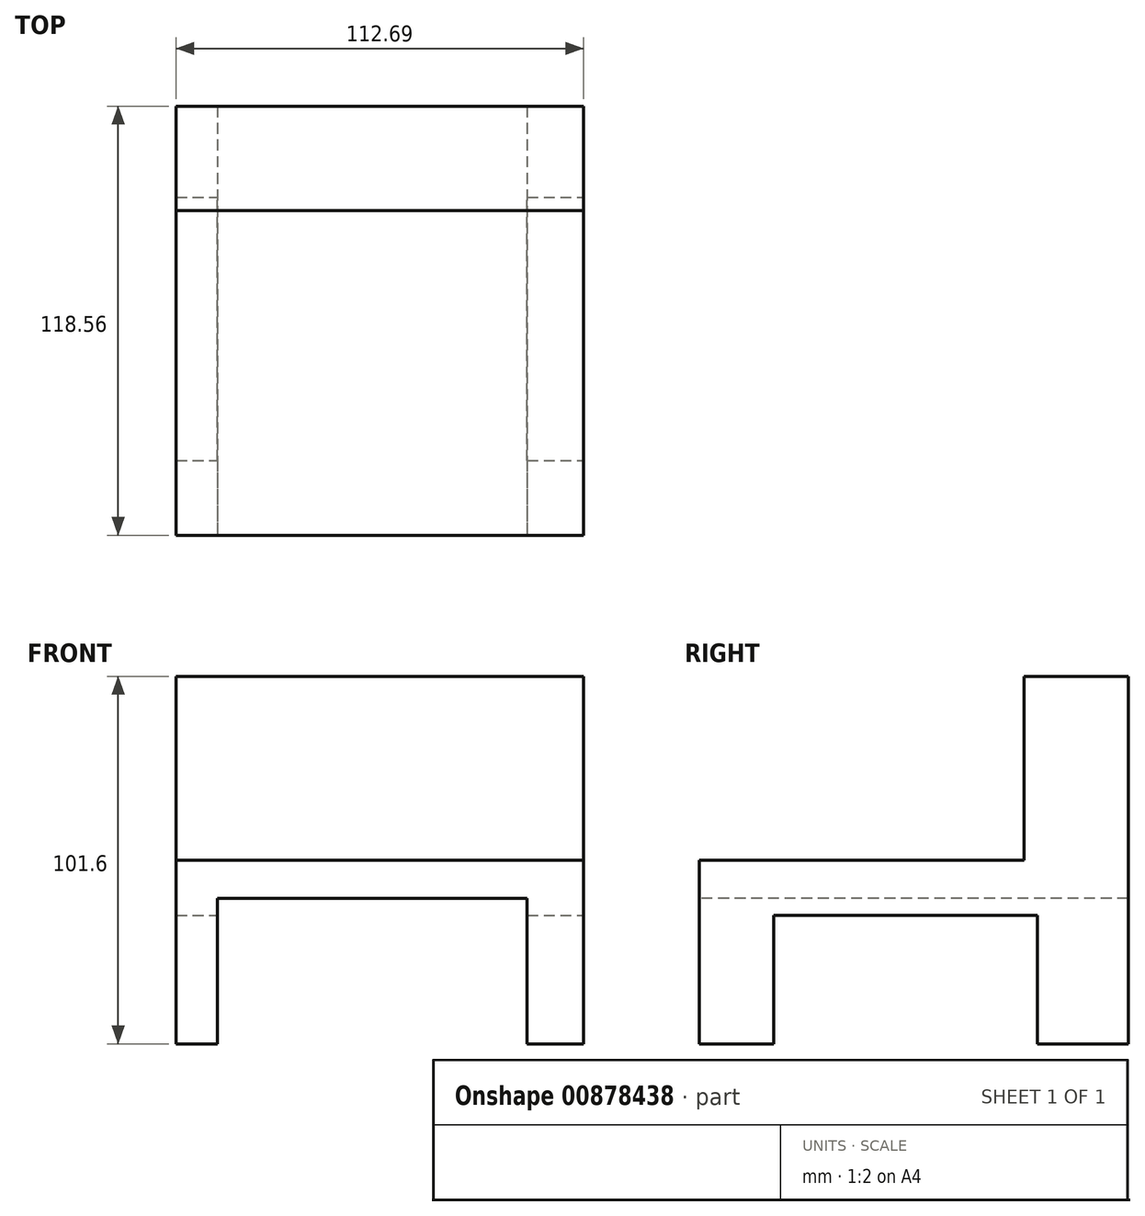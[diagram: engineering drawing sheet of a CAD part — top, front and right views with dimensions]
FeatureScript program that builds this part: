
annotation { "Feature Type Name" : "Feature", "Feature Type Description" : "" }
export const myFeature = defineFeature(function(context is Context, id is Id, definition is map)
    precondition{}
    {
        {
            var Q0;
            Q0=qCreatedBy(makeId("Top.planeOp"),FACE);
            var sketch = newSketch(context, id + "F0", { "sketchPlane" : qUnion([Q0])});
            skLineSegment(sketch, "E0.bottom", {"start": v(-59.67, -45.91) * mm, "end": v(53.02, -45.91) * mm});
            skLineSegment(sketch, "E0.top", {"start": v(-59.67, 72.65) * mm, "end": v(53.02, 72.65) * mm});
            skLineSegment(sketch, "E0.left", {"start": v(-59.67, -45.91) * mm, "end": v(-59.67, 72.65) * mm});
            skLineSegment(sketch, "E0.right", {"start": v(53.02, -45.91) * mm, "end": v(53.02, 72.65) * mm});
            skSolve(sketch);
        }
        {
            var Q0;
            Q0=makeQuery(id+"F0.imprint","IMPRINT",FACE,{"disambiguationData":[TD([[makeQuery(id+"F0.imprint","IMPRINT",EDGE,{"derivedFrom":sQuery(id+"F0.wireOp",EDGE,"E0.bottom")}),1.0]])]});
            extrude(context, id + "F1", {"entities" : qUnion([Q0]), "depth" : 101.6 * mm, "offsetDistance" : 25.4 * mm});
        }
        {
            var Q0;
            Q0=makeQuery(id+"F1.opExtrude","CAP_FACE",FACE,{"disambiguationData":[OSD([sQuery(id+"F0.wireOp",EDGE,"E0.bottom"),sQuery(id+"F0.wireOp",EDGE,"E0.top"),sQuery(id+"F0.wireOp",EDGE,"E0.left"),sQuery(id+"F0.wireOp",EDGE,"E0.right")])],"isStart":false});
            var sketch = newSketch(context, id + "F2", { "sketchPlane" : qUnion([Q0])});
            skLineSegment(sketch, "E1.bottom", {"start": v(-59.67, -45.91) * mm, "end": v(53.02, -45.91) * mm});
            skLineSegment(sketch, "E1.top", {"start": v(-59.67, 43.81) * mm, "end": v(53.02, 43.81) * mm});
            skLineSegment(sketch, "E1.left", {"start": v(-59.67, -45.91) * mm, "end": v(-59.67, 43.81) * mm});
            skLineSegment(sketch, "E1.right", {"start": v(53.02, -45.91) * mm, "end": v(53.02, 43.81) * mm});
            skSolve(sketch);
        }
        {
            var Q0;
            Q0=makeQuery(id+"F2.imprint","IMPRINT",FACE,{"disambiguationData":[TD([[makeQuery(id+"F2.imprint","IMPRINT",EDGE,{"derivedFrom":sQuery(id+"F2.wireOp",EDGE,"E1.bottom")}),1.0]])]});
            extrude(context, id + "F3", {"entities" : qUnion([Q0]), "operationType" : NewBodyOperationType.REMOVE, "oppositeDirection" : true, "depth" : 50.8 * mm, "offsetDistance" : 25.4 * mm});
        }
        {
            var Q0;
            Q0=makeQuery(id+"F1.opExtrude","SWEPT_FACE",FACE,{"disambiguationData":[OSD([sQuery(id+"F0.wireOp",EDGE,"E0.bottom")])]});
            var sketch = newSketch(context, id + "F4", { "sketchPlane" : qUnion([Q0])});
            skLineSegment(sketch, "E2.bottom", {"start": v(-48.2, 0) * mm, "end": v(37.4, 0) * mm});
            skLineSegment(sketch, "E2.top", {"start": v(-48.2, 40.25) * mm, "end": v(37.4, 40.25) * mm});
            skLineSegment(sketch, "E2.left", {"start": v(-48.2, 0) * mm, "end": v(-48.2, 40.25) * mm});
            skLineSegment(sketch, "E2.right", {"start": v(37.4, 0) * mm, "end": v(37.4, 40.25) * mm});
            skSolve(sketch);
        }
        {
            var Q0;
            Q0=makeQuery(id+"F4.imprint","IMPRINT",FACE,{"disambiguationData":[TD([[makeQuery(id+"F4.imprint","IMPRINT",EDGE,{"derivedFrom":sQuery(id+"F4.wireOp",EDGE,"E2.bottom")}),1.0]])]});
            extrude(context, id + "F5", {"entities" : qUnion([Q0]), "operationType" : NewBodyOperationType.REMOVE, "oppositeDirection" : true, "depth" : 127 * mm, "offsetDistance" : 25.4 * mm});
        }
        {
            var Q0;
            Q0=makeQuery(id+"F1.opExtrude","SWEPT_FACE",FACE,{"disambiguationData":[OSD([sQuery(id+"F0.wireOp",EDGE,"E0.right")])]});
            var sketch = newSketch(context, id + "F6", { "sketchPlane" : qUnion([Q0])});
            skLineSegment(sketch, "E3.bottom", {"start": v(-25.31, 0) * mm, "end": v(47.5, 0) * mm});
            skLineSegment(sketch, "E3.top", {"start": v(-25.31, 35.5) * mm, "end": v(47.5, 35.5) * mm});
            skLineSegment(sketch, "E3.left", {"start": v(-25.31, 0) * mm, "end": v(-25.31, 35.5) * mm});
            skLineSegment(sketch, "E3.right", {"start": v(47.5, 0) * mm, "end": v(47.5, 35.5) * mm});
            skSolve(sketch);
        }
        {
            var Q0;
            Q0=makeQuery(id+"F6.imprint","IMPRINT",FACE,{"disambiguationData":[TD([[makeQuery(id+"F6.imprint","IMPRINT",EDGE,{"derivedFrom":sQuery(id+"F6.wireOp",EDGE,"E3.bottom")}),1.0]])]});
            extrude(context, id + "F7", {"entities" : qUnion([Q0]), "operationType" : NewBodyOperationType.REMOVE, "oppositeDirection" : true, "depth" : 127 * mm, "offsetDistance" : 25.4 * mm});
        }
    });
